# Revit family: 3-528-xxx - 37-528-xxx - Magneta (Wall Sconce)
name_source: partatom
category: Lighting Fixtures
revit_build: Autodesk Revit 2018 (Build: 20180423_1000(x64)
units: mm (PartAtom-declared; Revit-internal decimal feet)

## family parameters
Cut with Voids When Loaded = No
Host = Face
Light Source = Yes
Part Type = Normal
Room Calculation Point = No
Round Connector Dimension = Use Diameter
Shared = No

## types (6) — shared parameters
Color Filter = 16777215
Dimming Lamp Color Temperature Shift = <None>
Emit from Line Length = 11 "
Lamp = LED Array
Manufacturer = Oxygen Lighting & Fans
Model = 3-528-xxx / 37-528-xxx - Magneta
Other = <By Category>
Photometric Web File = 3-528-24 Magneta Sconce.ies
Tilt Angle = 180.00°
URL = www.oxygenlighting.com
Wattage Comments = 15.2 W at 120 V
zero-valued in all types: Default Elevation

## per-type parameters (varying)
| type | Diffuser | Metal Finish |
| 3-528-14 / 37-528-14 - Magneta | Matte White Acrylic | 14 - Polished Chrome |
| 3-528-24 / 37-528-24 - Magneta | Matte White Acrylic | 24 - Satin Nickel |
| 3-528-40 / 37-528-40 - Magneta | Matte White Acrylic | 40 - Aged Brass |
| 3-528-140 / 37-528-140 - Magneta | White Opal Glass | 40 - Aged Brass |
| 3-528-124 / 37-528-124 - Magneta | White Opal Glass | 24 - Satin Nickel |
| 3-528-114 / 37-528-114 - Magneta | White Opal Glass | 14 - Polished Chrome |

## geometry (parser evidence)
native form markers: Sweep x5
no freeform markers — native parametric forms only
